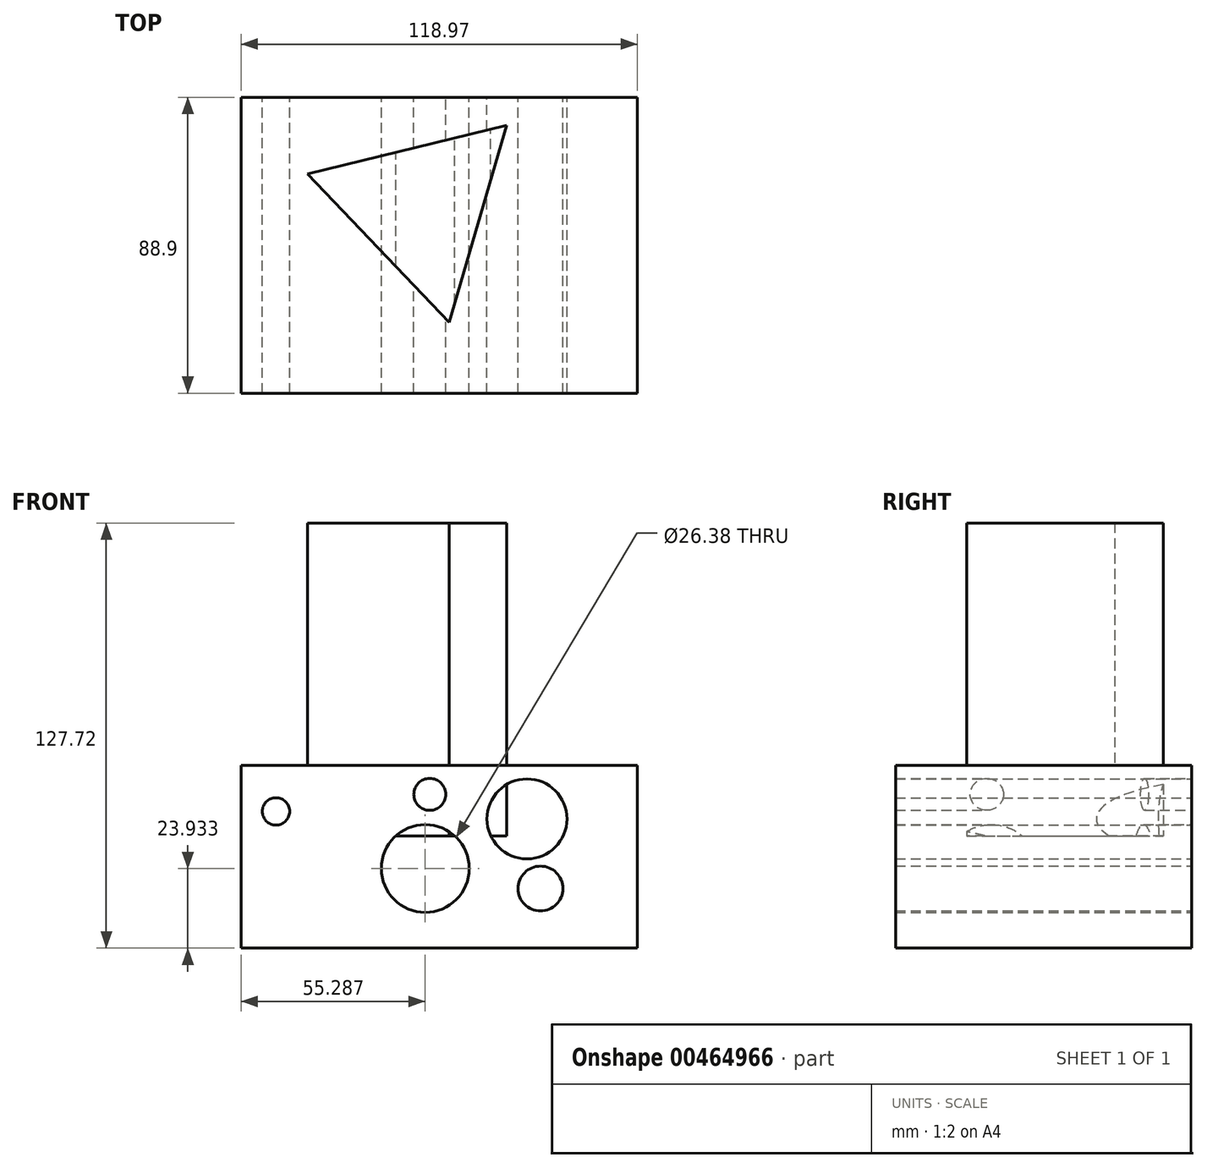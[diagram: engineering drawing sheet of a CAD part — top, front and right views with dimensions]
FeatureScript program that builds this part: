
annotation { "Feature Type Name" : "Feature", "Feature Type Description" : "" }
export const myFeature = defineFeature(function(context is Context, id is Id, definition is map)
    precondition{}
    {
        {
            var Q0;
            Q0=qCreatedBy(makeId("Front.planeOp"),FACE);
            var sketch = newSketch(context, id + "F0", { "sketchPlane" : qUnion([Q0])});
            skLineSegment(sketch, "E0.bottom", {"start": v(-39.48, 21.2) * mm, "end": v(79.5, 21.2) * mm});
            skLineSegment(sketch, "E0.top", {"start": v(-39.48, -33.74) * mm, "end": v(79.5, -33.74) * mm});
            skLineSegment(sketch, "E0.left", {"start": v(-39.48, 21.2) * mm, "end": v(-39.48, -33.74) * mm});
            skLineSegment(sketch, "E0.right", {"start": v(79.5, 21.2) * mm, "end": v(79.5, -33.74) * mm});
            skCircle(sketch, "E1", {"center": v(-29.04, 7.35) * mm, "radius": 4.1 * mm});
            skCircle(sketch, "E2", {"center": v(17.16, 12.46) * mm, "radius": 4.8 * mm});
            skCircle(sketch, "E3", {"center": v(15.8, -9.8) * mm, "radius": 13.2 * mm});
            skCircle(sketch, "E4", {"center": v(46.35, 5.1) * mm, "radius": 12.01 * mm});
            skCircle(sketch, "E5", {"center": v(50.42, -15.83) * mm, "radius": 6.72 * mm});
            skSolve(sketch);
        }
        {
            var Q0;
            Q0 = qSketchRegion(id + "F0", true);
            extrude(context, id + "F1", {"entities" : qUnion([Q0]), "depth" : 88.9 * mm});
        }
        {
            var Q0;
            Q0=qCreatedBy(makeId("Top.planeOp"),FACE);
            var sketch = newSketch(context, id + "F2", { "sketchPlane" : qUnion([Q0])});
            skCircle(sketch, "E6.cCircle", {"center": v(14.54, -33.04) * mm, "radius": 17.78 * mm, "construction": true});
            skLineSegment(sketch, "E6.0", {"start": v(40.22, -8.44) * mm, "end": v(23, -67.58) * mm});
            skLineSegment(sketch, "E6.1", {"start": v(23, -67.58) * mm, "end": v(-19.6, -23.1) * mm});
            skLineSegment(sketch, "E6.2", {"start": v(-19.6, -23.1) * mm, "end": v(40.22, -8.44) * mm});
            skPoint(sketch, "E6.0.midPoint", {"position": v(31.61, -38) * mm});
            skSolve(sketch);
        }
        {
            var Q0;
            Q0 = qSketchRegion(id + "F2", true);
            extrude(context, id + "F3", {"entities" : qUnion([Q0]), "operationType" : NewBodyOperationType.ADD, "depth" : 93.98 * mm});
        }
    });
